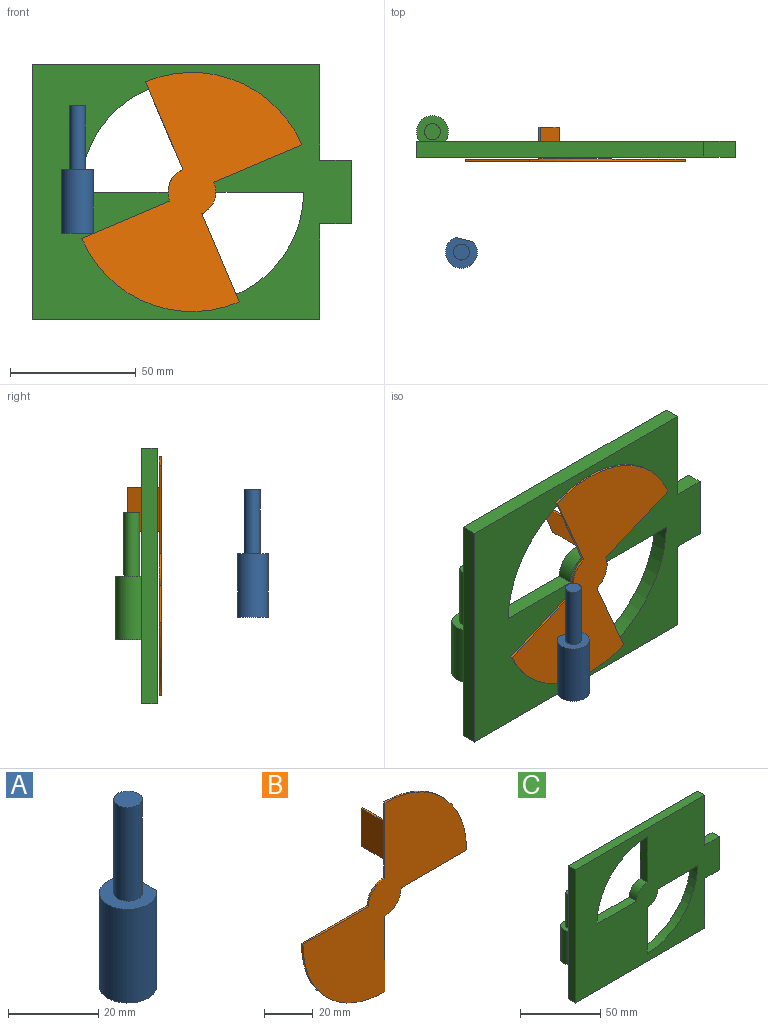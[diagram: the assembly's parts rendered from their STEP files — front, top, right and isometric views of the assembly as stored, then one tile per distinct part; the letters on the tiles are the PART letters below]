
ASSEMBLY  parts=3 mates=1
PART A: 6 faces, bbox 11.4x12.7x50.8 mm
  f0: cylinder r=3.17mm len=25.4mm, axis (0,0,-1), area 506.7mm2, adj f1,f4
  f1: plane 6.35x6.35mm, normal (0,0,1), area 31.7mm2, adj f0
  f2: plane 25.4x7.62mm, normal (1,0,0), area 193.5mm2, adj f3,f4,f5
  f3: cylinder r=6.35mm len=25.4mm, axis (0,0,-1), area 805.8mm2, adj f2,f4,f5
  f4: plane 12.7x11.43mm, normal (0,0,1), area 88.4mm2, adj f0,f2,f3
  f5: plane 12.7x11.43mm, normal (0,0,-1), area 120.1mm2, adj f2,f3
PART B: 16 faces, bbox 95.3x13.5x95.2 mm
  f0: plane 95.25x95.25mm, normal (0,1,0), area 3692.2mm2, adj f1,f2,f3,f4,f5,f6,f7,f8
  f1: plane 38.1x0.83mm, normal (1,0,0), area 31.5mm2, adj f0,f2,f8,f9
  f2: cylinder r=9.53mm len=9.62mm, axis (0,1,0), area 12.3mm2, adj f0,f1,f3,f9
  f3: plane 38.1x0.83mm, normal (0,0,-1), area 31.5mm2, adj f0,f2,f4,f9
  f4: cylinder r=47.62mm len=47.53mm, axis (0,1,0), area 61.6mm2, adj f0,f3,f5,f9
  f5: plane 38.1x0.83mm, normal (-1,0,0), area 31.5mm2, adj f0,f4,f6,f9,f11
  f6: cylinder r=9.53mm len=9.66mm, axis (0,1,0), area 12.4mm2, adj f0,f5,f7,f9
  f7: plane 38.1x0.83mm, normal (0,0,1), area 31.5mm2, adj f0,f6,f8,f9
  f8: cylinder r=47.62mm len=47.76mm, axis (0,1,0), area 61.9mm2, adj f0,f1,f7,f9
  f9: plane 95.25x95.25mm, normal (0,-1,0), area 3705.3mm2, adj f1,f2,f3,f4,f5,f6,f7,f8
  f10: plane 12.7x0.83mm, normal (0,0,1), area 10.5mm2, adj f0,f11,f13,f14,f15
  f11: plane 19.05x0.14mm, normal (0,-1,0), area 2.6mm2, adj f5,f10,f12,f15
  f12: plane 12.7x0.83mm, normal (0,0,-1), area 10.5mm2, adj f0,f11,f13,f14,f15
  f13: plane 19.05x0.83mm, normal (0,1,0), area 15.7mm2, adj f10,f12,f14,f15
  f14: plane 19.05x12.7mm, normal (1,0,0), area 241.9mm2, adj f0,f10,f12,f13
  f15: plane 19.05x12.7mm, normal (-1,0,0), area 241.9mm2, adj f10,f11,f12,f13
PART C: 23 faces, bbox 127x16.5x101.6 mm
  f0: plane 127x101.6mm, normal (0,1,0), area 8720.5mm2, adj f1,f2,f3,f4,f5,f6,f7,f8
  f1: plane 38.1x6.35mm, normal (1,0,0), area 241.9mm2, adj f0,f2,f15,f16
  f2: plane 12.7x6.35mm, normal (0,0,-1), area 80.6mm2, adj f0,f1,f3,f16
  f3: plane 25.4x6.35mm, normal (1,0,0), area 161.3mm2, adj f0,f2,f4,f16
  f4: plane 12.7x6.35mm, normal (0,0,1), area 80.6mm2, adj f0,f3,f5,f16
  f5: plane 38.1x6.35mm, normal (1,0,0), area 241.9mm2, adj f0,f4,f6,f16
  f6: plane 114.3x6.35mm, normal (0,0,1), area 725.8mm2, adj f0,f5,f16,f17
  f7: plane 34.93x6.35mm, normal (0,0,1), area 221.8mm2, adj f0,f8,f13,f16
  f8: cylinder r=44.45mm len=44.45mm, axis (0,1,0), area 443.4mm2, adj f0,f7,f9,f16
  f9: plane 34.93x6.35mm, normal (-1,0,0), area 221.8mm2, adj f0,f8,f13,f16
  f10: cylinder r=44.45mm len=44.45mm, axis (0,1,0), area 442.6mm2, adj f0,f11,f14,f16
  f11: plane 34.93x6.35mm, normal (1,0,0), area 221.8mm2, adj f0,f10,f12,f16
  f12: cylinder r=9.53mm len=9.52mm, axis (0,1,0), area 94.2mm2, adj f0,f11,f14,f16
  f13: cylinder r=9.53mm len=9.53mm, axis (0,1,0), area 95mm2, adj f0,f7,f9,f16
  f14: plane 34.93x6.35mm, normal (0,0,-1), area 221.8mm2, adj f0,f10,f12,f16
  f15: plane 114.3x6.35mm, normal (0,0,-1), area 725.8mm2, adj f0,f1,f16,f17
  f16: plane 127x101.6mm, normal (0,-1,0), area 8978.6mm2, adj f1,f2,f3,f4,f5,f6,f7,f8
  f17: plane 101.6x6.35mm, normal (-1,0,0), area 645.2mm2, adj f0,f6,f15,f16
  f18: cylinder r=6.35mm len=25.4mm, axis (0,0,1), area 714.3mm2, adj f0,f19,f20
  f19: plane 12.7x10.16mm, normal (0,0,-1), area 108.6mm2, adj f0,f18
  f20: plane 12.7x10.16mm, normal (0,0,1), area 77mm2, adj f0,f18,f21
  f21: cylinder r=3.17mm len=25.4mm, axis (0,0,-1), area 506.7mm2, adj f20,f22
  f22: plane 6.35x6.35mm, normal (0,0,1), area 31.7mm2, adj f21
PLACE A rot(axis=(0,0,1),76.2deg) t=(-44.19,-41.76,-15.22)mm
PLACE B rot(axis=(0,-1,0),23.1deg) t=(1.44,-4.74,1.23)mm
PLACE C t=(1.44,2.37,1.23)mm
MATE revolute B.f4 <-> C.f10  axis (0,-1,0) through (1.44,-5.56,1.23)mm
